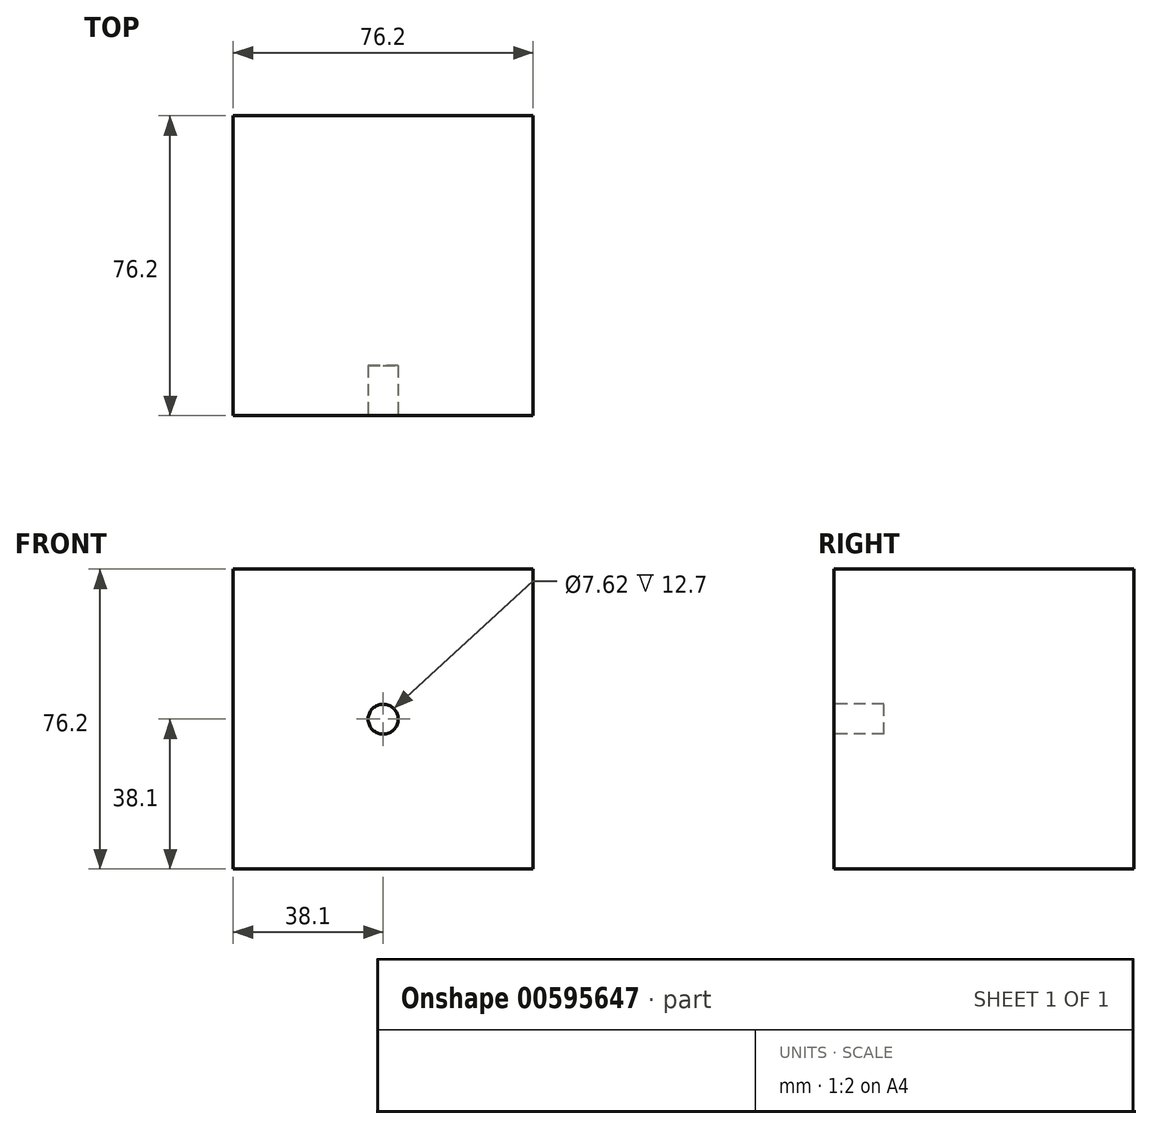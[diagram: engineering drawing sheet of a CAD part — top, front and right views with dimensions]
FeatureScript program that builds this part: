
annotation { "Feature Type Name" : "Feature", "Feature Type Description" : "" }
export const myFeature = defineFeature(function(context is Context, id is Id, definition is map)
    precondition{}
    {
        {
            var Q0;
            Q0=qCreatedBy(makeId("Front.planeOp"),FACE);
            var sketch = newSketch(context, id + "F0", { "sketchPlane" : qUnion([Q0])});
            skLineSegment(sketch, "E0.bottom", {"start": v(-38.1, 38.1) * mm, "end": v(38.1, 38.1) * mm});
            skLineSegment(sketch, "E0.top", {"start": v(-38.1, -38.1) * mm, "end": v(38.1, -38.1) * mm});
            skLineSegment(sketch, "E0.left", {"start": v(-38.1, 38.1) * mm, "end": v(-38.1, -38.1) * mm});
            skLineSegment(sketch, "E0.right", {"start": v(38.1, 38.1) * mm, "end": v(38.1, -38.1) * mm});
            skPoint(sketch, "E0.middle", {"position": v(0, 0) * mm});
            skSolve(sketch);
        }
        {
            var Q0;
            Q0 = qSketchRegion(id + "F0", true);
            extrude(context, id + "F1", {"entities" : qUnion([Q0]), "depth" : 76.2 * mm, "offsetDistance" : 25.4 * mm});
        }
        {
            var Q0;
            Q0=makeQuery(id+"F1.opExtrude","CAP_FACE",FACE,{"disambiguationData":[OSD([sQuery(id+"F0.wireOp",EDGE,"E0.bottom"),sQuery(id+"F0.wireOp",EDGE,"E0.top"),sQuery(id+"F0.wireOp",EDGE,"E0.left"),sQuery(id+"F0.wireOp",EDGE,"E0.right")])],"isStart":false});
            var sketch = newSketch(context, id + "F2", { "sketchPlane" : qUnion([Q0])});
            skCircle(sketch, "E1", {"center": v(0, 0) * mm, "radius": 3.81 * mm});
            skSolve(sketch);
        }
        {
            var Q0;
            Q0 = qSketchRegion(id + "F2", true);
            extrude(context, id + "F3", {"entities" : qUnion([Q0]), "operationType" : NewBodyOperationType.REMOVE, "oppositeDirection" : true, "depth" : 12.7 * mm, "offsetDistance" : 25.4 * mm});
        }
    });
